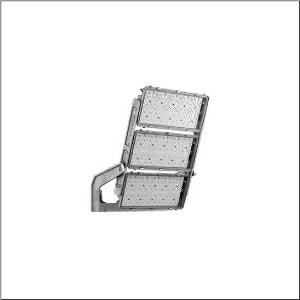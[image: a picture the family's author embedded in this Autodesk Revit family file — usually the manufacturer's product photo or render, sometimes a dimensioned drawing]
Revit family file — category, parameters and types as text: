
# Revit family: floodlight_fl_11_maxi_pro_remote___pl43_5xa779524a01ba_c92a
name_source: partatom
category: Lighting Fixtures
units: mm (PartAtom-declared; Revit-internal decimal feet)

## family parameters
Cut with Voids When Loaded = No
Host = Face
Light Source = No
Part Type = Normal
Room Calculation Point = No
Round Connector Dimension = Use Diameter
Shared = No

## types (1)
- --- (1 x LED, 108940 lm, 1020.5 W, 5700K)
    Apparent Load = 1020 VA
    CIE Flux Codes = 25 74 99 100 100
    Color Rendering = 90
    Color Temperature = 5700K
    Default Elevation = 1800 mm
    Description = Floodlight FL 11  maxi  pro Remote floodlight; light control with lens of PMMA; cover panel of toughened safety glass, transparent; light distribution: PL43, asymmetric direct distribution, LEDcolour temperature: 5700K, rated luminous flux: 108.940lm, colour rendering: CRI > 90, light colour: 957; luminous efficacy: 107lm/W; brightness control: DMX+RDM; with terminal, 8-pole, max. 2.5mm², mains connection: 220..240V/380..400V AC, 50/60Hz, surge voltage resistance: line to ground: 10kV, ECG replaceable separately, LED unit replaceable without ESD environment, dustproof LED module, dimming range 10..100%; 1021W floodlight with 3x LED unit of diecast aluminium, coated grey; length: 713mm / width: 651mm / height: 338mm; mounting bracket, of diecast aluminium, uncoated, natural, equipment: Longlife, protection rating (complete): IP66; insulation class (complete): insulation class I (protective earthing); certification: CE, ENEC, VDE; ball protection: ball impact resistance with accessories, impact resistance: IK07; only for outdoor installations, rated ambient temperature 10°C, permissible operating ambient temperature: -40..+40°C, permissible storage temperature: -40..+85°Cpackaging unit: 1 piece

Light Distribution: PL43
    Height = 320 mm
    Lamp = 1 x LED
    Lamp Light Flux = 108940 lm
    Lamp Power = 1020.5 W
    Lamp count = 1
    Length = 1002 mm
    Luminous efficacy = 107 lm/W
    Manufacturer = Siteco
    ModVariant = No
    Model = 5XA779524A01BA
    Mounting Place = Ceiling
    Mounting Type = Surface mounted
    Number of Poles = 1
    OnlyDefault = Yes
    Power Factor = 1
    Product Name = Floodlight FL 11 maxi pro Remote | PL43
    Product group = floodlight | ceiling mounted
    ProductGroupID = 301
    Protection Class = Protection class I
    Protection Degree = IP 66
    RLX_Detail_Level = 1
    RLX_Emergency_Light_Flux = 0 lm
    RLX_Emergency_Type = 0
    RLX_Emergency_Type_DB = No
    RlxData = <blob elided: 53157 chars, md5=b160854a>
    Socket = socket
    Standby Power = 0 W
    System Light Flux = 108940 lm
    System Power = 1020 W
    Type Comments = factory setting: luminous flux: 100 % | dim-lin: 255 | 710 mA
    Type Image = l_1349141.jpg
    URL = http://relux.com
    VarID = @adj_096554
    Voltage = 0 V
    Weight = 0.00 kg
    Width = 655 mm

## geometry (parser evidence)
native form markers: Blend x4, Sweep x12
no freeform markers — native parametric forms only
